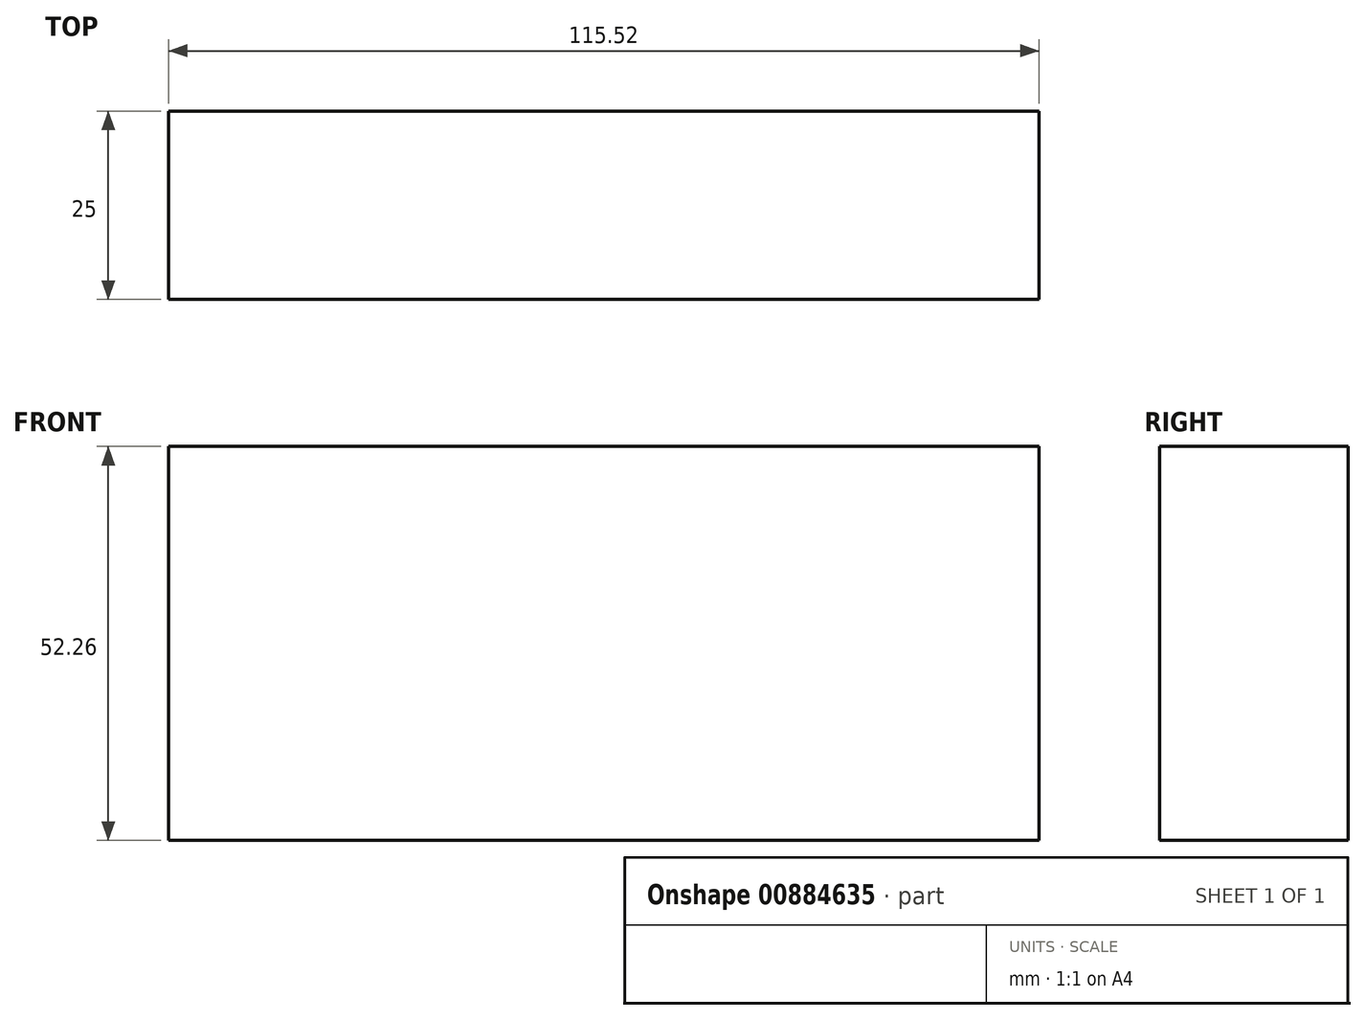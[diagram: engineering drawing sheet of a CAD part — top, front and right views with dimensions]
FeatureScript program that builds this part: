
annotation { "Feature Type Name" : "Feature", "Feature Type Description" : "" }
export const myFeature = defineFeature(function(context is Context, id is Id, definition is map)
    precondition{}
    {
        {
            var Q0;
            Q0=qCreatedBy(makeId("Front.planeOp"),FACE);
            var sketch = newSketch(context, id + "F0", { "sketchPlane" : qUnion([Q0])});
            skLineSegment(sketch, "E0.bottom", {"start": v(-54.95, 26.13) * mm, "end": v(60.57, 26.13) * mm});
            skLineSegment(sketch, "E0.top", {"start": v(-54.95, -26.13) * mm, "end": v(60.57, -26.13) * mm});
            skLineSegment(sketch, "E0.left", {"start": v(-54.95, 26.13) * mm, "end": v(-54.95, -26.13) * mm});
            skLineSegment(sketch, "E0.right", {"start": v(60.57, 26.13) * mm, "end": v(60.57, -26.13) * mm});
            skSolve(sketch);
        }
        {
            var Q0;
            Q0 = qSketchRegion(id + "F0", true);
            var Q1;
            Q1=makeQuery(id+"F0.imprint","IMPRINT",FACE,{"disambiguationData":[TD([[makeQuery(id+"F0.imprint","IMPRINT",EDGE,{"derivedFrom":sQuery(id+"F0.wireOp",EDGE,"E0.bottom")}),-1.0]])]});
            extrude(context, id + "F1", {"entities" : qUnion([Q0, Q1]), "depth" : 25 * mm, "offsetDistance" : 25 * mm});
        }
    });
